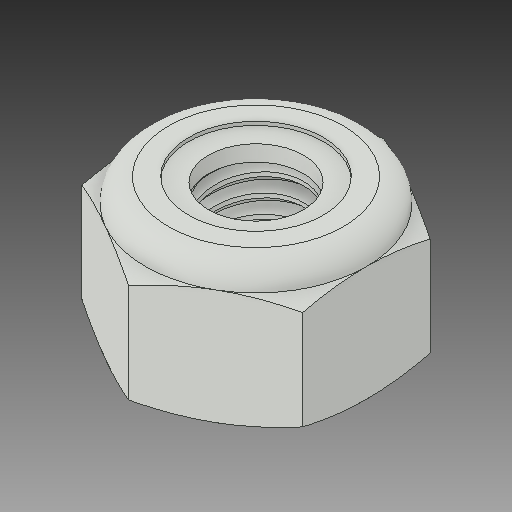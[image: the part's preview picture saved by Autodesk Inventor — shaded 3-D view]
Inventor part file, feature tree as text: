
AUTODESK INVENTOR PART (.ipt)
format: ipt  version: 2019 (Build 230136000, 136)  size: 332,800 bytes
history: native  units: in
note: dims shown in document units (in); Inventor stores cm internally (conversion verified against a paired STEP export)
features: other x1, revolve x1
ambient origin geometry x8: Origin, YZ Plane, XZ Plane, XY Plane, X Axis, Y Axis, Z Axis, Center Point
bodies: Solid1 (feature_tree), Solid2 (feature_tree)
feature tree (2):
  other  "Cut-Revolve4"
  revolve  "Revolve2"  [1 undecoded]
note: 1 required parameter value undecoded (feature->parameter linkage not recoverable at this tier; creation-order binding heuristic only, values carry confidence <= 0.55)
